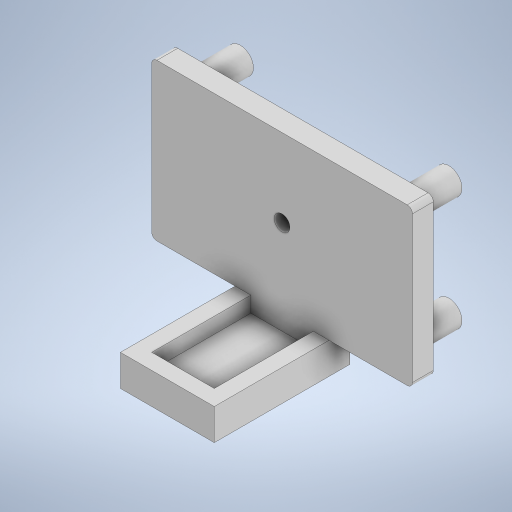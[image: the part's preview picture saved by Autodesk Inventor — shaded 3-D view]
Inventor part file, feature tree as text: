
AUTODESK INVENTOR PART (.ipt)
format: ipt  version: 2023 (Build 270158000, 158)  size: 293,888 bytes
history: native  units: in
note: dims shown in document units (in); Inventor stores cm internally (conversion verified against a paired STEP export)
features: sketch x7, extrude x4, fillet x2, hole x1
ambient origin geometry x8: Origin, YZ Plane, XZ Plane, XY Plane, X Axis, Y Axis, Z Axis, Center Point
bodies: Solid1 (feature_tree)
feature tree (14):
  extrude  "Extrusion1"  Depth=1.1811in
  fillet  "Fillet1"  Radius=0.1575in
  fillet  "Fillet2"  Radius=0.0394in
  hole  "Hole2"  [1 undecoded]
  sketch  "Sketch6"  dims[d20=0.1181in d21=0.2362in d22=0.1575in d23=0.0787in d24=90.0deg d25=0.315in d26=0.8108in d27=0.1969in]
  sketch  "Sketch18"  dims[d28=0.1969in d29=0.1969in]
  extrude  "Extrusion10"  Depth=0.315in
  extrude  "Extrusion11"  Depth=0.1969in
  sketch  "Sketch20"  dims[d39=0.1969in]
  extrude  "Extrusion12"  Depth=0.1969in
  sketch  "Sketch1"  dims[d0=1.9685in d1=1.1811in d2=0.1575in d3=0.0in d4=0.0394in]
  sketch  "Sketch4"  dims[d5=0.0394in d19=0.1181in]
  sketch  "Sketch19"  dims[d30=0.1969in d38=0.1969in]
  sketch  "Sketch21"  dims[d40=0.1969in d41=0.1969in d42=0.1575in d43=0.1575in d44=0.1575in d45=0.1575in d82=0.4724in d83=0.0in d84=0.7087in d85=0.2362in d86=1.0236in d87=0.0in d88=0.4724in d89=0.748in d90=0.1181in d91=0.0in d7=0.0394in d8=0.0394in d9=0.0394in d10=0.0059in d11=0.0098in d12=0.0148in d13=0.5635in d14=0.0295in d15=0.8108in d16=0.0025in d17=0.0295in d18=0.0148in d31=0.0394in d32=0.0394in d33=0.0394in d34=0.0059in d35=0.0098in d36=0.0148in d37=0.5635in d73=0.0in d74=0.0in d75=0.0in d76=0.0in d77=0.0344in d78=0.0197in d79=0.0344in d92=0.0295in d93=0.0148in]
note: 1 required parameter value undecoded (feature->parameter linkage not recoverable at this tier; creation-order binding heuristic only, values carry confidence <= 0.55)
